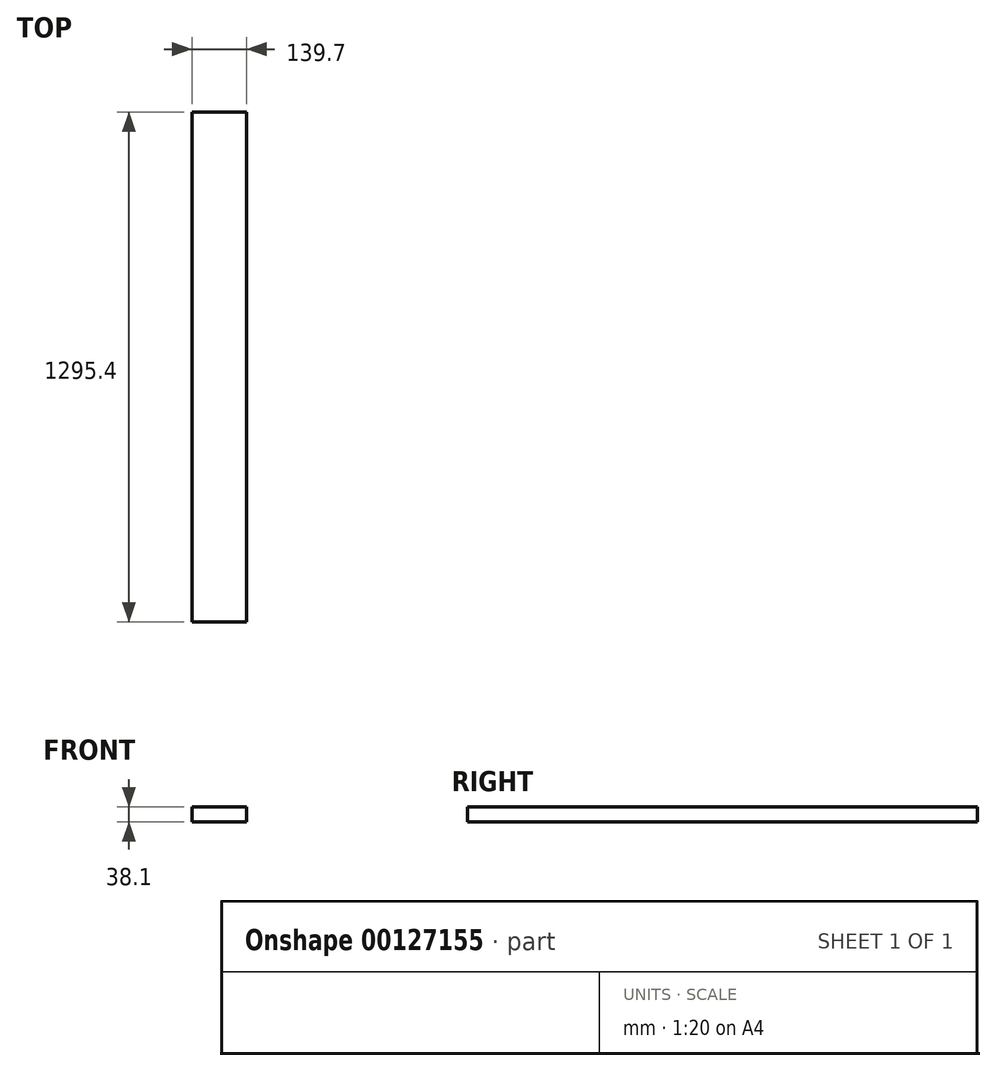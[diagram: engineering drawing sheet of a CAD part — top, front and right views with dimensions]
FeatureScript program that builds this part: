
annotation { "Feature Type Name" : "Feature", "Feature Type Description" : "" }
export const myFeature = defineFeature(function(context is Context, id is Id, definition is map)
    precondition{}
    {
        {
            var Q0;
            Q0=qCreatedBy(makeId("Front.planeOp"),FACE);
            var sketch = newSketch(context, id + "F0", { "sketchPlane" : qUnion([Q0])});
            skLineSegment(sketch, "E0.bottom", {"start": v(69.85, -19.05) * mm, "end": v(-69.85, -19.05) * mm});
            skLineSegment(sketch, "E0.top", {"start": v(69.85, 19.05) * mm, "end": v(-69.85, 19.05) * mm});
            skLineSegment(sketch, "E0.left", {"start": v(69.85, -19.05) * mm, "end": v(69.85, 19.05) * mm});
            skLineSegment(sketch, "E0.right", {"start": v(-69.85, -19.05) * mm, "end": v(-69.85, 19.05) * mm});
            skPoint(sketch, "E0.middle", {"position": v(0, 0) * mm});
            skSolve(sketch);
        }
        {
            var Q0;
            Q0=qSketchRegion(id+"F0",true);
            extrude(context, id + "F1", {"entities" : qUnion([Q0]), "depth" : 1295.4 * mm, "offsetDistance" : 25.4 * mm});
        }
    });
